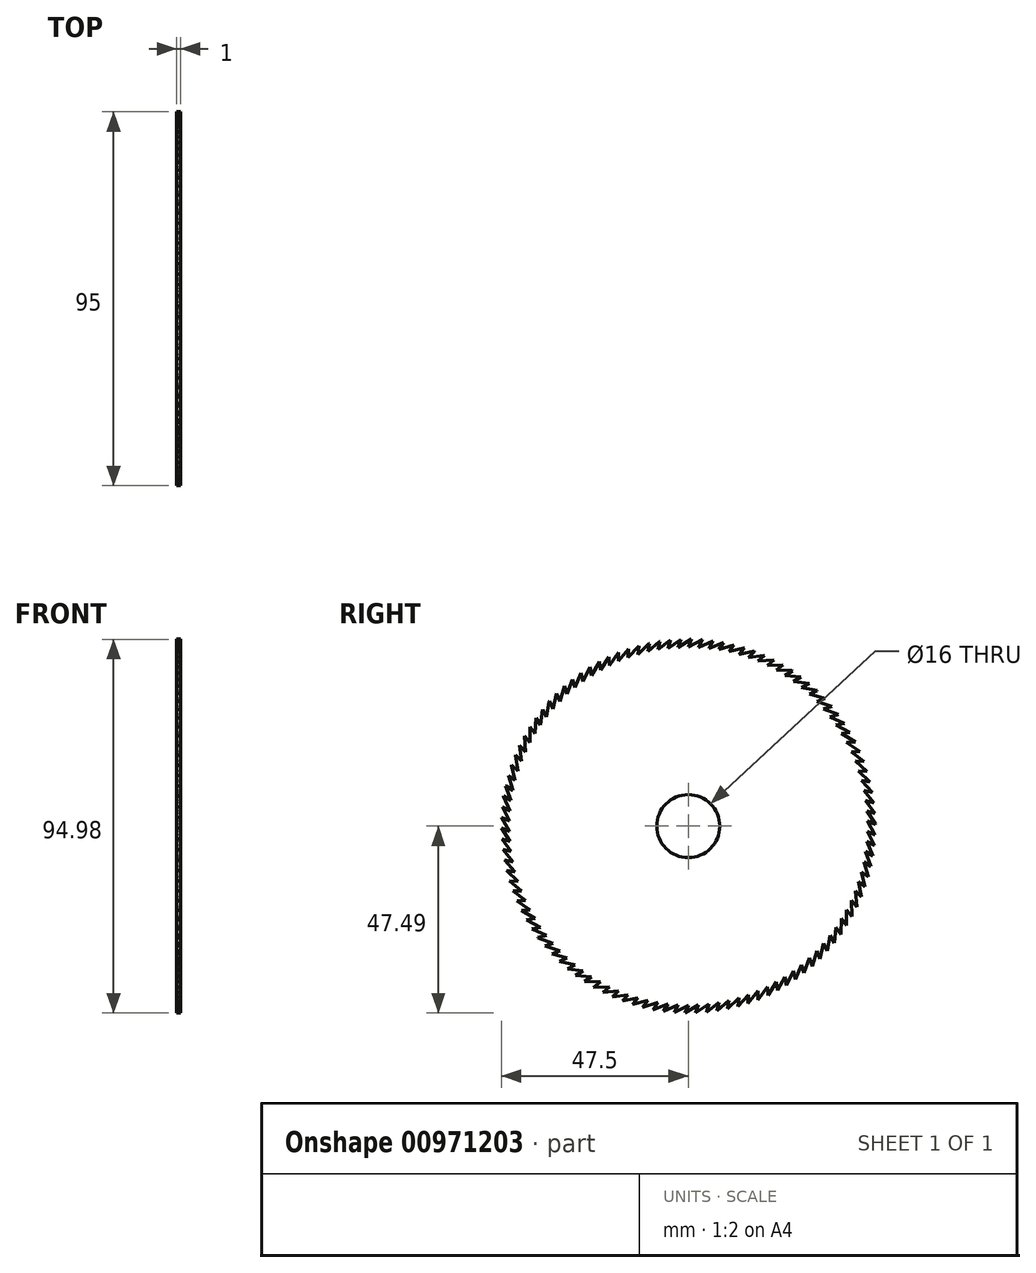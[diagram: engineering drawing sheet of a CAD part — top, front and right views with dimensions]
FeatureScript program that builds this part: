
annotation { "Feature Type Name" : "Feature", "Feature Type Description" : "" }
export const myFeature = defineFeature(function(context is Context, id is Id, definition is map)
    precondition{}
    {
        {
            var Q0;
            Q0=qCreatedBy(makeId("Right.planeOp"),FACE);
            var sketch = newSketch(context, id + "F0", { "sketchPlane" : qUnion([Q0])});
            skCircle(sketch, "E0", {"center": v(0, 0) * mm, "radius": 47.5 * mm});
            skCircle(sketch, "E1", {"center": v(0, 0) * mm, "radius": 8 * mm});
            skCircle(sketch, "E2", {"center": v(0, 0) * mm, "radius": 45.5 * mm, "construction": true});
            skLineSegment(sketch, "E3", {"start": v(0, 45.5) * mm, "end": v(0.86, 47.5) * mm});
            skLineSegment(sketch, "E4", {"start": v(0, 45.5) * mm, "end": v(3.56, 47.37) * mm});
            skArc(sketch, "E5", {"start": v(3.56, 47.37) * mm, "mid": v(2.21, 47.46) * mm, "end": v(0.86, 47.5) * mm});
            skLineSegment(sketch, "E6.1.0", {"start": v(-2.6, 45.43) * mm, "end": v(-1.85, 47.46) * mm});
            skArc(sketch, "E6.1.1", {"start": v(0.85, 47.5) * mm, "mid": v(-0.5, 47.51) * mm, "end": v(-1.85, 47.46) * mm});
            skLineSegment(sketch, "E6.1.2", {"start": v(-2.6, 45.43) * mm, "end": v(0.85, 47.5) * mm});
            skLineSegment(sketch, "E6.2.0", {"start": v(-5.19, 45.2) * mm, "end": v(-4.56, 47.28) * mm});
            skArc(sketch, "E6.2.1", {"start": v(-1.86, 47.46) * mm, "mid": v(-3.21, 47.4) * mm, "end": v(-4.56, 47.28) * mm});
            skLineSegment(sketch, "E6.2.2", {"start": v(-5.19, 45.2) * mm, "end": v(-1.86, 47.46) * mm});
            skLineSegment(sketch, "E6.3.0", {"start": v(-7.76, 44.83) * mm, "end": v(-7.25, 46.94) * mm});
            skArc(sketch, "E6.3.1", {"start": v(-4.57, 47.28) * mm, "mid": v(-5.91, 47.14) * mm, "end": v(-7.25, 46.94) * mm});
            skLineSegment(sketch, "E6.3.2", {"start": v(-7.76, 44.83) * mm, "end": v(-4.57, 47.28) * mm});
            skLineSegment(sketch, "E6.4.0", {"start": v(-10.3, 44.32) * mm, "end": v(-9.92, 46.45) * mm});
            skArc(sketch, "E6.4.1", {"start": v(-7.26, 46.94) * mm, "mid": v(-8.6, 46.73) * mm, "end": v(-9.92, 46.45) * mm});
            skLineSegment(sketch, "E6.4.2", {"start": v(-10.3, 44.32) * mm, "end": v(-7.26, 46.94) * mm});
            skLineSegment(sketch, "E6.5.0", {"start": v(-12.82, 43.66) * mm, "end": v(-12.55, 45.81) * mm});
            skArc(sketch, "E6.5.1", {"start": v(-9.93, 46.45) * mm, "mid": v(-11.25, 46.16) * mm, "end": v(-12.55, 45.81) * mm});
            skLineSegment(sketch, "E6.5.2", {"start": v(-12.82, 43.66) * mm, "end": v(-9.93, 46.45) * mm});
            skLineSegment(sketch, "E6.6.0", {"start": v(-15.3, 42.85) * mm, "end": v(-15.15, 45.02) * mm});
            skArc(sketch, "E6.6.1", {"start": v(-12.57, 45.8) * mm, "mid": v(-13.87, 45.45) * mm, "end": v(-15.15, 45.02) * mm});
            skLineSegment(sketch, "E6.6.2", {"start": v(-15.3, 42.85) * mm, "end": v(-12.57, 45.8) * mm});
            skLineSegment(sketch, "E6.7.0", {"start": v(-17.71, 41.91) * mm, "end": v(-17.7, 44.08) * mm});
            skArc(sketch, "E6.7.1", {"start": v(-15.16, 45.02) * mm, "mid": v(-16.44, 44.58) * mm, "end": v(-17.7, 44.08) * mm});
            skLineSegment(sketch, "E6.7.2", {"start": v(-17.71, 41.91) * mm, "end": v(-15.16, 45.02) * mm});
            skLineSegment(sketch, "E6.8.0", {"start": v(-20.08, 40.83) * mm, "end": v(-20.18, 43) * mm});
            skArc(sketch, "E6.8.1", {"start": v(-17.7, 44.08) * mm, "mid": v(-18.96, 43.57) * mm, "end": v(-20.18, 43) * mm});
            skLineSegment(sketch, "E6.8.2", {"start": v(-20.08, 40.83) * mm, "end": v(-17.7, 44.08) * mm});
            skLineSegment(sketch, "E6.9.0", {"start": v(-22.37, 39.62) * mm, "end": v(-22.6, 41.78) * mm});
            skArc(sketch, "E6.9.1", {"start": v(-20.2, 43) * mm, "mid": v(-21.41, 42.42) * mm, "end": v(-22.6, 41.78) * mm});
            skLineSegment(sketch, "E6.9.2", {"start": v(-22.37, 39.62) * mm, "end": v(-20.2, 43) * mm});
            skLineSegment(sketch, "E6.10.0", {"start": v(-24.6, 38.28) * mm, "end": v(-24.95, 40.42) * mm});
            skArc(sketch, "E6.10.1", {"start": v(-22.61, 41.77) * mm, "mid": v(-23.8, 41.12) * mm, "end": v(-24.95, 40.42) * mm});
            skLineSegment(sketch, "E6.10.2", {"start": v(-24.6, 38.28) * mm, "end": v(-22.61, 41.77) * mm});
            skLineSegment(sketch, "E6.11.0", {"start": v(-26.74, 36.81) * mm, "end": v(-27.22, 38.93) * mm});
            skArc(sketch, "E6.11.1", {"start": v(-24.96, 40.41) * mm, "mid": v(-26.1, 39.7) * mm, "end": v(-27.22, 38.93) * mm});
            skLineSegment(sketch, "E6.11.2", {"start": v(-26.74, 36.81) * mm, "end": v(-24.96, 40.41) * mm});
            skLineSegment(sketch, "E6.12.0", {"start": v(-28.8, 35.22) * mm, "end": v(-29.4, 37.31) * mm});
            skArc(sketch, "E6.12.1", {"start": v(-27.23, 38.92) * mm, "mid": v(-28.33, 38.14) * mm, "end": v(-29.4, 37.31) * mm});
            skLineSegment(sketch, "E6.12.2", {"start": v(-28.8, 35.22) * mm, "end": v(-27.23, 38.92) * mm});
            skLineSegment(sketch, "E6.13.0", {"start": v(-30.77, 33.52) * mm, "end": v(-31.48, 35.57) * mm});
            skArc(sketch, "E6.13.1", {"start": v(-29.4, 37.3) * mm, "mid": v(-30.46, 36.46) * mm, "end": v(-31.48, 35.57) * mm});
            skLineSegment(sketch, "E6.13.2", {"start": v(-30.77, 33.52) * mm, "end": v(-29.4, 37.3) * mm});
            skLineSegment(sketch, "E6.14.0", {"start": v(-32.63, 31.71) * mm, "end": v(-33.46, 33.72) * mm});
            skArc(sketch, "E6.14.1", {"start": v(-31.49, 35.56) * mm, "mid": v(-32.5, 34.66) * mm, "end": v(-33.46, 33.72) * mm});
            skLineSegment(sketch, "E6.14.2", {"start": v(-32.63, 31.71) * mm, "end": v(-31.49, 35.56) * mm});
            skLineSegment(sketch, "E6.15.0", {"start": v(-34.39, 29.8) * mm, "end": v(-35.33, 31.75) * mm});
            skArc(sketch, "E6.15.1", {"start": v(-33.47, 33.7) * mm, "mid": v(-34.42, 32.75) * mm, "end": v(-35.33, 31.75) * mm});
            skLineSegment(sketch, "E6.15.2", {"start": v(-34.39, 29.8) * mm, "end": v(-33.47, 33.7) * mm});
            skLineSegment(sketch, "E6.16.0", {"start": v(-36.03, 27.78) * mm, "end": v(-37.08, 29.69) * mm});
            skArc(sketch, "E6.16.1", {"start": v(-35.34, 31.74) * mm, "mid": v(-36.23, 30.73) * mm, "end": v(-37.08, 29.69) * mm});
            skLineSegment(sketch, "E6.16.2", {"start": v(-36.03, 27.78) * mm, "end": v(-35.34, 31.74) * mm});
            skLineSegment(sketch, "E6.17.0", {"start": v(-37.56, 25.68) * mm, "end": v(-38.72, 27.52) * mm});
            skArc(sketch, "E6.17.1", {"start": v(-37.1, 29.67) * mm, "mid": v(-37.93, 28.62) * mm, "end": v(-38.72, 27.52) * mm});
            skLineSegment(sketch, "E6.17.2", {"start": v(-37.56, 25.68) * mm, "end": v(-37.1, 29.67) * mm});
            skLineSegment(sketch, "E6.18.0", {"start": v(-38.96, 23.5) * mm, "end": v(-40.22, 25.26) * mm});
            skArc(sketch, "E6.18.1", {"start": v(-38.72, 27.5) * mm, "mid": v(-39.5, 26.4) * mm, "end": v(-40.22, 25.26) * mm});
            skLineSegment(sketch, "E6.18.2", {"start": v(-38.96, 23.5) * mm, "end": v(-38.72, 27.5) * mm});
            skLineSegment(sketch, "E6.19.0", {"start": v(-40.24, 21.23) * mm, "end": v(-41.6, 22.93) * mm});
            skArc(sketch, "E6.19.1", {"start": v(-40.23, 25.25) * mm, "mid": v(-40.94, 24.1) * mm, "end": v(-41.6, 22.93) * mm});
            skLineSegment(sketch, "E6.19.2", {"start": v(-40.24, 21.23) * mm, "end": v(-40.23, 25.25) * mm});
            skLineSegment(sketch, "E6.20.0", {"start": v(-41.39, 18.9) * mm, "end": v(-42.84, 20.51) * mm});
            skArc(sketch, "E6.20.1", {"start": v(-41.6, 22.91) * mm, "mid": v(-42.25, 21.73) * mm, "end": v(-42.84, 20.51) * mm});
            skLineSegment(sketch, "E6.20.2", {"start": v(-41.39, 18.9) * mm, "end": v(-41.6, 22.91) * mm});
            skLineSegment(sketch, "E6.21.0", {"start": v(-42.4, 16.5) * mm, "end": v(-43.94, 18.04) * mm});
            skArc(sketch, "E6.21.1", {"start": v(-42.85, 20.5) * mm, "mid": v(-43.43, 19.28) * mm, "end": v(-43.94, 18.04) * mm});
            skLineSegment(sketch, "E6.21.2", {"start": v(-42.4, 16.5) * mm, "end": v(-42.85, 20.5) * mm});
            skLineSegment(sketch, "E6.22.0", {"start": v(-43.27, 14.06) * mm, "end": v(-44.9, 15.5) * mm});
            skArc(sketch, "E6.22.1", {"start": v(-43.95, 18.02) * mm, "mid": v(-44.45, 16.77) * mm, "end": v(-44.9, 15.5) * mm});
            skLineSegment(sketch, "E6.22.2", {"start": v(-43.27, 14.06) * mm, "end": v(-43.95, 18.02) * mm});
            skLineSegment(sketch, "E6.23.0", {"start": v(-44, 11.57) * mm, "end": v(-45.71, 12.9) * mm});
            skArc(sketch, "E6.23.1", {"start": v(-44.9, 15.48) * mm, "mid": v(-45.34, 14.2) * mm, "end": v(-45.71, 12.9) * mm});
            skLineSegment(sketch, "E6.23.2", {"start": v(-44, 11.57) * mm, "end": v(-44.9, 15.48) * mm});
            skLineSegment(sketch, "E6.24.0", {"start": v(-44.6, 9.04) * mm, "end": v(-46.37, 10.28) * mm});
            skArc(sketch, "E6.24.1", {"start": v(-45.72, 12.9) * mm, "mid": v(-46.08, 11.6) * mm, "end": v(-46.37, 10.28) * mm});
            skLineSegment(sketch, "E6.24.2", {"start": v(-44.6, 9.04) * mm, "end": v(-45.72, 12.9) * mm});
            skLineSegment(sketch, "E6.25.0", {"start": v(-45.04, 6.48) * mm, "end": v(-46.89, 7.61) * mm});
            skArc(sketch, "E6.25.1", {"start": v(-46.38, 10.26) * mm, "mid": v(-46.66, 8.95) * mm, "end": v(-46.89, 7.61) * mm});
            skLineSegment(sketch, "E6.25.2", {"start": v(-45.04, 6.48) * mm, "end": v(-46.38, 10.26) * mm});
            skLineSegment(sketch, "E6.26.0", {"start": v(-45.33, 3.9) * mm, "end": v(-47.24, 4.92) * mm});
            skArc(sketch, "E6.26.1", {"start": v(-46.89, 7.6) * mm, "mid": v(-47.1, 6.27) * mm, "end": v(-47.24, 4.92) * mm});
            skLineSegment(sketch, "E6.26.2", {"start": v(-45.33, 3.9) * mm, "end": v(-46.89, 7.6) * mm});
            skLineSegment(sketch, "E6.27.0", {"start": v(-45.48, 1.3) * mm, "end": v(-47.45, 2.22) * mm});
            skArc(sketch, "E6.27.1", {"start": v(-47.25, 4.91) * mm, "mid": v(-47.38, 3.57) * mm, "end": v(-47.45, 2.22) * mm});
            skLineSegment(sketch, "E6.27.2", {"start": v(-45.48, 1.3) * mm, "end": v(-47.25, 4.91) * mm});
            skLineSegment(sketch, "E6.28.0", {"start": v(-45.48, -1.3) * mm, "end": v(-47.5, -0.5) * mm});
            skArc(sketch, "E6.28.1", {"start": v(-47.45, 2.2) * mm, "mid": v(-47.5, 0.86) * mm, "end": v(-47.5, -0.5) * mm});
            skLineSegment(sketch, "E6.28.2", {"start": v(-45.48, -1.3) * mm, "end": v(-47.45, 2.2) * mm});
            skLineSegment(sketch, "E6.29.0", {"start": v(-45.33, -3.9) * mm, "end": v(-47.4, -3.2) * mm});
            skArc(sketch, "E6.29.1", {"start": v(-47.5, -0.5) * mm, "mid": v(-47.48, -1.86) * mm, "end": v(-47.4, -3.2) * mm});
            skLineSegment(sketch, "E6.29.2", {"start": v(-45.33, -3.9) * mm, "end": v(-47.5, -0.5) * mm});
            skLineSegment(sketch, "E6.30.0", {"start": v(-45.04, -6.48) * mm, "end": v(-47.13, -5.9) * mm});
            skArc(sketch, "E6.30.1", {"start": v(-47.4, -3.22) * mm, "mid": v(-47.3, -4.56) * mm, "end": v(-47.13, -5.9) * mm});
            skLineSegment(sketch, "E6.30.2", {"start": v(-45.04, -6.48) * mm, "end": v(-47.4, -3.22) * mm});
            skLineSegment(sketch, "E6.31.0", {"start": v(-44.6, -9.04) * mm, "end": v(-46.72, -8.58) * mm});
            skArc(sketch, "E6.31.1", {"start": v(-47.13, -5.92) * mm, "mid": v(-46.96, -7.26) * mm, "end": v(-46.72, -8.58) * mm});
            skLineSegment(sketch, "E6.31.2", {"start": v(-44.6, -9.04) * mm, "end": v(-47.13, -5.92) * mm});
            skLineSegment(sketch, "E6.32.0", {"start": v(-44, -11.57) * mm, "end": v(-46.15, -11.24) * mm});
            skArc(sketch, "E6.32.1", {"start": v(-46.72, -8.6) * mm, "mid": v(-46.47, -9.93) * mm, "end": v(-46.15, -11.24) * mm});
            skLineSegment(sketch, "E6.32.2", {"start": v(-44, -11.57) * mm, "end": v(-46.72, -8.6) * mm});
            skLineSegment(sketch, "E6.33.0", {"start": v(-43.27, -14.06) * mm, "end": v(-45.43, -13.85) * mm});
            skArc(sketch, "E6.33.1", {"start": v(-46.15, -11.25) * mm, "mid": v(-45.82, -12.56) * mm, "end": v(-45.43, -13.85) * mm});
            skLineSegment(sketch, "E6.33.2", {"start": v(-43.27, -14.06) * mm, "end": v(-46.15, -11.25) * mm});
            skLineSegment(sketch, "E6.34.0", {"start": v(-42.4, -16.5) * mm, "end": v(-44.57, -16.43) * mm});
            skArc(sketch, "E6.34.1", {"start": v(-45.43, -13.87) * mm, "mid": v(-45.03, -15.16) * mm, "end": v(-44.57, -16.43) * mm});
            skLineSegment(sketch, "E6.34.2", {"start": v(-42.4, -16.5) * mm, "end": v(-45.43, -13.87) * mm});
            skLineSegment(sketch, "E6.35.0", {"start": v(-41.39, -18.9) * mm, "end": v(-43.56, -18.94) * mm});
            skArc(sketch, "E6.35.1", {"start": v(-44.56, -16.44) * mm, "mid": v(-44.1, -17.7) * mm, "end": v(-43.56, -18.94) * mm});
            skLineSegment(sketch, "E6.35.2", {"start": v(-41.39, -18.9) * mm, "end": v(-44.56, -16.44) * mm});
            skLineSegment(sketch, "E6.36.0", {"start": v(-40.24, -21.23) * mm, "end": v(-42.4, -21.4) * mm});
            skArc(sketch, "E6.36.1", {"start": v(-43.55, -18.96) * mm, "mid": v(-43, -20.2) * mm, "end": v(-42.4, -21.4) * mm});
            skLineSegment(sketch, "E6.36.2", {"start": v(-40.24, -21.23) * mm, "end": v(-43.55, -18.96) * mm});
            skLineSegment(sketch, "E6.37.0", {"start": v(-38.96, -23.5) * mm, "end": v(-41.12, -23.78) * mm});
            skArc(sketch, "E6.37.1", {"start": v(-42.4, -21.41) * mm, "mid": v(-41.79, -22.61) * mm, "end": v(-41.12, -23.78) * mm});
            skLineSegment(sketch, "E6.37.2", {"start": v(-38.96, -23.5) * mm, "end": v(-42.4, -21.41) * mm});
            skLineSegment(sketch, "E6.38.0", {"start": v(-37.56, -25.68) * mm, "end": v(-39.7, -26.1) * mm});
            skArc(sketch, "E6.38.1", {"start": v(-41.1, -23.8) * mm, "mid": v(-40.43, -24.96) * mm, "end": v(-39.7, -26.1) * mm});
            skLineSegment(sketch, "E6.38.2", {"start": v(-37.56, -25.68) * mm, "end": v(-41.1, -23.8) * mm});
            skLineSegment(sketch, "E6.39.0", {"start": v(-36.03, -27.78) * mm, "end": v(-38.14, -28.32) * mm});
            skArc(sketch, "E6.39.1", {"start": v(-39.68, -26.1) * mm, "mid": v(-38.94, -27.23) * mm, "end": v(-38.14, -28.32) * mm});
            skLineSegment(sketch, "E6.39.2", {"start": v(-36.03, -27.78) * mm, "end": v(-39.68, -26.1) * mm});
            skLineSegment(sketch, "E6.40.0", {"start": v(-34.39, -29.8) * mm, "end": v(-36.46, -30.45) * mm});
            skArc(sketch, "E6.40.1", {"start": v(-38.13, -28.33) * mm, "mid": v(-37.32, -29.4) * mm, "end": v(-36.46, -30.45) * mm});
            skLineSegment(sketch, "E6.40.2", {"start": v(-34.39, -29.8) * mm, "end": v(-38.13, -28.33) * mm});
            skLineSegment(sketch, "E6.41.0", {"start": v(-32.63, -31.71) * mm, "end": v(-34.66, -32.48) * mm});
            skArc(sketch, "E6.41.1", {"start": v(-36.45, -30.46) * mm, "mid": v(-35.58, -31.5) * mm, "end": v(-34.66, -32.48) * mm});
            skLineSegment(sketch, "E6.41.2", {"start": v(-32.63, -31.71) * mm, "end": v(-36.45, -30.46) * mm});
            skLineSegment(sketch, "E6.42.0", {"start": v(-30.77, -33.52) * mm, "end": v(-32.75, -34.4) * mm});
            skArc(sketch, "E6.42.1", {"start": v(-34.65, -32.5) * mm, "mid": v(-33.72, -33.47) * mm, "end": v(-32.75, -34.4) * mm});
            skLineSegment(sketch, "E6.42.2", {"start": v(-30.77, -33.52) * mm, "end": v(-34.65, -32.5) * mm});
            skLineSegment(sketch, "E6.43.0", {"start": v(-28.8, -35.22) * mm, "end": v(-30.73, -36.22) * mm});
            skArc(sketch, "E6.43.1", {"start": v(-32.74, -34.42) * mm, "mid": v(-31.76, -35.34) * mm, "end": v(-30.73, -36.22) * mm});
            skLineSegment(sketch, "E6.43.2", {"start": v(-28.8, -35.22) * mm, "end": v(-32.74, -34.42) * mm});
            skLineSegment(sketch, "E6.44.0", {"start": v(-26.74, -36.81) * mm, "end": v(-28.61, -37.91) * mm});
            skArc(sketch, "E6.44.1", {"start": v(-30.72, -36.23) * mm, "mid": v(-29.69, -37.1) * mm, "end": v(-28.61, -37.91) * mm});
            skLineSegment(sketch, "E6.44.2", {"start": v(-26.74, -36.81) * mm, "end": v(-30.72, -36.23) * mm});
            skLineSegment(sketch, "E6.45.0", {"start": v(-24.6, -38.28) * mm, "end": v(-26.4, -39.49) * mm});
            skArc(sketch, "E6.45.1", {"start": v(-28.6, -37.92) * mm, "mid": v(-27.52, -38.73) * mm, "end": v(-26.4, -39.49) * mm});
            skLineSegment(sketch, "E6.45.2", {"start": v(-24.6, -38.28) * mm, "end": v(-28.6, -37.92) * mm});
            skLineSegment(sketch, "E6.46.0", {"start": v(-22.37, -39.62) * mm, "end": v(-24.1, -40.93) * mm});
            skArc(sketch, "E6.46.1", {"start": v(-26.4, -39.5) * mm, "mid": v(-25.27, -40.24) * mm, "end": v(-24.1, -40.93) * mm});
            skLineSegment(sketch, "E6.46.2", {"start": v(-22.37, -39.62) * mm, "end": v(-26.4, -39.5) * mm});
            skLineSegment(sketch, "E6.47.0", {"start": v(-20.08, -40.83) * mm, "end": v(-21.73, -42.24) * mm});
            skArc(sketch, "E6.47.1", {"start": v(-24.1, -40.94) * mm, "mid": v(-22.93, -41.62) * mm, "end": v(-21.73, -42.24) * mm});
            skLineSegment(sketch, "E6.47.2", {"start": v(-20.08, -40.83) * mm, "end": v(-24.1, -40.94) * mm});
            skLineSegment(sketch, "E6.48.0", {"start": v(-17.71, -41.91) * mm, "end": v(-19.28, -43.4) * mm});
            skArc(sketch, "E6.48.1", {"start": v(-21.72, -42.24) * mm, "mid": v(-20.51, -42.86) * mm, "end": v(-19.28, -43.4) * mm});
            skLineSegment(sketch, "E6.48.2", {"start": v(-17.71, -41.91) * mm, "end": v(-21.72, -42.24) * mm});
            skLineSegment(sketch, "E6.49.0", {"start": v(-15.3, -42.85) * mm, "end": v(-16.77, -44.44) * mm});
            skArc(sketch, "E6.49.1", {"start": v(-19.27, -43.42) * mm, "mid": v(-18.03, -43.96) * mm, "end": v(-16.77, -44.44) * mm});
            skLineSegment(sketch, "E6.49.2", {"start": v(-15.3, -42.85) * mm, "end": v(-19.27, -43.42) * mm});
            skLineSegment(sketch, "E6.50.0", {"start": v(-12.82, -43.66) * mm, "end": v(-14.2, -45.32) * mm});
            skArc(sketch, "E6.50.1", {"start": v(-16.76, -44.45) * mm, "mid": v(-15.5, -44.92) * mm, "end": v(-14.2, -45.32) * mm});
            skLineSegment(sketch, "E6.50.2", {"start": v(-12.82, -43.66) * mm, "end": v(-16.76, -44.45) * mm});
            skLineSegment(sketch, "E6.51.0", {"start": v(-10.3, -44.32) * mm, "end": v(-11.6, -46.06) * mm});
            skArc(sketch, "E6.51.1", {"start": v(-14.2, -45.33) * mm, "mid": v(-12.9, -45.73) * mm, "end": v(-11.6, -46.06) * mm});
            skLineSegment(sketch, "E6.51.2", {"start": v(-10.3, -44.32) * mm, "end": v(-14.2, -45.33) * mm});
            skLineSegment(sketch, "E6.52.0", {"start": v(-7.76, -44.83) * mm, "end": v(-8.95, -46.65) * mm});
            skArc(sketch, "E6.52.1", {"start": v(-11.58, -46.07) * mm, "mid": v(-10.27, -46.39) * mm, "end": v(-8.95, -46.65) * mm});
            skLineSegment(sketch, "E6.52.2", {"start": v(-7.76, -44.83) * mm, "end": v(-11.58, -46.07) * mm});
            skLineSegment(sketch, "E6.53.0", {"start": v(-5.19, -45.2) * mm, "end": v(-6.27, -47.08) * mm});
            skArc(sketch, "E6.53.1", {"start": v(-8.94, -46.65) * mm, "mid": v(-7.6, -46.9) * mm, "end": v(-6.27, -47.08) * mm});
            skLineSegment(sketch, "E6.53.2", {"start": v(-5.19, -45.2) * mm, "end": v(-8.94, -46.65) * mm});
            skLineSegment(sketch, "E6.54.0", {"start": v(-2.6, -45.43) * mm, "end": v(-3.57, -47.37) * mm});
            skArc(sketch, "E6.54.1", {"start": v(-6.26, -47.09) * mm, "mid": v(-4.92, -47.26) * mm, "end": v(-3.57, -47.37) * mm});
            skLineSegment(sketch, "E6.54.2", {"start": v(-2.6, -45.43) * mm, "end": v(-6.26, -47.09) * mm});
            skLineSegment(sketch, "E6.55.0", {"start": v(0, -45.5) * mm, "end": v(-0.86, -47.5) * mm});
            skArc(sketch, "E6.55.1", {"start": v(-3.56, -47.37) * mm, "mid": v(-2.21, -47.46) * mm, "end": v(-0.86, -47.5) * mm});
            skLineSegment(sketch, "E6.55.2", {"start": v(0, -45.5) * mm, "end": v(-3.56, -47.37) * mm});
            skLineSegment(sketch, "E6.56.0", {"start": v(2.6, -45.43) * mm, "end": v(1.85, -47.46) * mm});
            skArc(sketch, "E6.56.1", {"start": v(-0.85, -47.5) * mm, "mid": v(0.5, -47.51) * mm, "end": v(1.85, -47.46) * mm});
            skLineSegment(sketch, "E6.56.2", {"start": v(2.6, -45.43) * mm, "end": v(-0.85, -47.5) * mm});
            skLineSegment(sketch, "E6.57.0", {"start": v(5.19, -45.2) * mm, "end": v(4.56, -47.28) * mm});
            skArc(sketch, "E6.57.1", {"start": v(1.86, -47.46) * mm, "mid": v(3.21, -47.4) * mm, "end": v(4.56, -47.28) * mm});
            skLineSegment(sketch, "E6.57.2", {"start": v(5.19, -45.2) * mm, "end": v(1.86, -47.46) * mm});
            skLineSegment(sketch, "E6.58.0", {"start": v(7.76, -44.83) * mm, "end": v(7.25, -46.94) * mm});
            skArc(sketch, "E6.58.1", {"start": v(4.57, -47.28) * mm, "mid": v(5.91, -47.14) * mm, "end": v(7.25, -46.94) * mm});
            skLineSegment(sketch, "E6.58.2", {"start": v(7.76, -44.83) * mm, "end": v(4.57, -47.28) * mm});
            skLineSegment(sketch, "E6.59.0", {"start": v(10.3, -44.32) * mm, "end": v(9.92, -46.45) * mm});
            skArc(sketch, "E6.59.1", {"start": v(7.26, -46.94) * mm, "mid": v(8.6, -46.73) * mm, "end": v(9.92, -46.45) * mm});
            skLineSegment(sketch, "E6.59.2", {"start": v(10.3, -44.32) * mm, "end": v(7.26, -46.94) * mm});
            skLineSegment(sketch, "E6.60.0", {"start": v(12.82, -43.66) * mm, "end": v(12.55, -45.81) * mm});
            skArc(sketch, "E6.60.1", {"start": v(9.93, -46.45) * mm, "mid": v(11.25, -46.16) * mm, "end": v(12.55, -45.81) * mm});
            skLineSegment(sketch, "E6.60.2", {"start": v(12.82, -43.66) * mm, "end": v(9.93, -46.45) * mm});
            skLineSegment(sketch, "E6.61.0", {"start": v(15.3, -42.85) * mm, "end": v(15.15, -45.02) * mm});
            skArc(sketch, "E6.61.1", {"start": v(12.57, -45.8) * mm, "mid": v(13.87, -45.45) * mm, "end": v(15.15, -45.02) * mm});
            skLineSegment(sketch, "E6.61.2", {"start": v(15.3, -42.85) * mm, "end": v(12.57, -45.8) * mm});
            skLineSegment(sketch, "E6.62.0", {"start": v(17.71, -41.91) * mm, "end": v(17.7, -44.08) * mm});
            skArc(sketch, "E6.62.1", {"start": v(15.16, -45.02) * mm, "mid": v(16.44, -44.58) * mm, "end": v(17.7, -44.08) * mm});
            skLineSegment(sketch, "E6.62.2", {"start": v(17.71, -41.91) * mm, "end": v(15.16, -45.02) * mm});
            skLineSegment(sketch, "E6.63.0", {"start": v(20.08, -40.83) * mm, "end": v(20.18, -43) * mm});
            skArc(sketch, "E6.63.1", {"start": v(17.7, -44.08) * mm, "mid": v(18.96, -43.57) * mm, "end": v(20.18, -43) * mm});
            skLineSegment(sketch, "E6.63.2", {"start": v(20.08, -40.83) * mm, "end": v(17.7, -44.08) * mm});
            skLineSegment(sketch, "E6.64.0", {"start": v(22.37, -39.62) * mm, "end": v(22.6, -41.78) * mm});
            skArc(sketch, "E6.64.1", {"start": v(20.2, -43) * mm, "mid": v(21.41, -42.42) * mm, "end": v(22.6, -41.78) * mm});
            skLineSegment(sketch, "E6.64.2", {"start": v(22.37, -39.62) * mm, "end": v(20.2, -43) * mm});
            skLineSegment(sketch, "E6.65.0", {"start": v(24.6, -38.28) * mm, "end": v(24.95, -40.42) * mm});
            skArc(sketch, "E6.65.1", {"start": v(22.61, -41.77) * mm, "mid": v(23.8, -41.12) * mm, "end": v(24.95, -40.42) * mm});
            skLineSegment(sketch, "E6.65.2", {"start": v(24.6, -38.28) * mm, "end": v(22.61, -41.77) * mm});
            skLineSegment(sketch, "E6.66.0", {"start": v(26.74, -36.81) * mm, "end": v(27.22, -38.93) * mm});
            skArc(sketch, "E6.66.1", {"start": v(24.96, -40.41) * mm, "mid": v(26.1, -39.7) * mm, "end": v(27.22, -38.93) * mm});
            skLineSegment(sketch, "E6.66.2", {"start": v(26.74, -36.81) * mm, "end": v(24.96, -40.41) * mm});
            skLineSegment(sketch, "E6.67.0", {"start": v(28.8, -35.22) * mm, "end": v(29.4, -37.31) * mm});
            skArc(sketch, "E6.67.1", {"start": v(27.23, -38.92) * mm, "mid": v(28.33, -38.14) * mm, "end": v(29.4, -37.31) * mm});
            skLineSegment(sketch, "E6.67.2", {"start": v(28.8, -35.22) * mm, "end": v(27.23, -38.92) * mm});
            skLineSegment(sketch, "E6.68.0", {"start": v(30.77, -33.52) * mm, "end": v(31.48, -35.57) * mm});
            skArc(sketch, "E6.68.1", {"start": v(29.4, -37.3) * mm, "mid": v(30.46, -36.46) * mm, "end": v(31.48, -35.57) * mm});
            skLineSegment(sketch, "E6.68.2", {"start": v(30.77, -33.52) * mm, "end": v(29.4, -37.3) * mm});
            skLineSegment(sketch, "E6.69.0", {"start": v(32.63, -31.71) * mm, "end": v(33.46, -33.72) * mm});
            skArc(sketch, "E6.69.1", {"start": v(31.49, -35.56) * mm, "mid": v(32.5, -34.66) * mm, "end": v(33.46, -33.72) * mm});
            skLineSegment(sketch, "E6.69.2", {"start": v(32.63, -31.71) * mm, "end": v(31.49, -35.56) * mm});
            skLineSegment(sketch, "E6.70.0", {"start": v(34.39, -29.8) * mm, "end": v(35.33, -31.75) * mm});
            skArc(sketch, "E6.70.1", {"start": v(33.47, -33.7) * mm, "mid": v(34.42, -32.75) * mm, "end": v(35.33, -31.75) * mm});
            skLineSegment(sketch, "E6.70.2", {"start": v(34.39, -29.8) * mm, "end": v(33.47, -33.7) * mm});
            skLineSegment(sketch, "E6.71.0", {"start": v(36.03, -27.78) * mm, "end": v(37.08, -29.69) * mm});
            skArc(sketch, "E6.71.1", {"start": v(35.34, -31.74) * mm, "mid": v(36.23, -30.73) * mm, "end": v(37.08, -29.69) * mm});
            skLineSegment(sketch, "E6.71.2", {"start": v(36.03, -27.78) * mm, "end": v(35.34, -31.74) * mm});
            skLineSegment(sketch, "E6.72.0", {"start": v(37.56, -25.68) * mm, "end": v(38.72, -27.52) * mm});
            skArc(sketch, "E6.72.1", {"start": v(37.1, -29.67) * mm, "mid": v(37.93, -28.62) * mm, "end": v(38.72, -27.52) * mm});
            skLineSegment(sketch, "E6.72.2", {"start": v(37.56, -25.68) * mm, "end": v(37.1, -29.67) * mm});
            skLineSegment(sketch, "E6.73.0", {"start": v(38.96, -23.5) * mm, "end": v(40.22, -25.26) * mm});
            skArc(sketch, "E6.73.1", {"start": v(38.72, -27.5) * mm, "mid": v(39.5, -26.4) * mm, "end": v(40.22, -25.26) * mm});
            skLineSegment(sketch, "E6.73.2", {"start": v(38.96, -23.5) * mm, "end": v(38.72, -27.5) * mm});
            skLineSegment(sketch, "E6.74.0", {"start": v(40.24, -21.23) * mm, "end": v(41.6, -22.93) * mm});
            skArc(sketch, "E6.74.1", {"start": v(40.23, -25.25) * mm, "mid": v(40.94, -24.1) * mm, "end": v(41.6, -22.93) * mm});
            skLineSegment(sketch, "E6.74.2", {"start": v(40.24, -21.23) * mm, "end": v(40.23, -25.25) * mm});
            skLineSegment(sketch, "E6.75.0", {"start": v(41.39, -18.9) * mm, "end": v(42.84, -20.51) * mm});
            skArc(sketch, "E6.75.1", {"start": v(41.6, -22.91) * mm, "mid": v(42.25, -21.73) * mm, "end": v(42.84, -20.51) * mm});
            skLineSegment(sketch, "E6.75.2", {"start": v(41.39, -18.9) * mm, "end": v(41.6, -22.91) * mm});
            skLineSegment(sketch, "E6.76.0", {"start": v(42.4, -16.5) * mm, "end": v(43.94, -18.04) * mm});
            skArc(sketch, "E6.76.1", {"start": v(42.85, -20.5) * mm, "mid": v(43.43, -19.28) * mm, "end": v(43.94, -18.04) * mm});
            skLineSegment(sketch, "E6.76.2", {"start": v(42.4, -16.5) * mm, "end": v(42.85, -20.5) * mm});
            skLineSegment(sketch, "E6.77.0", {"start": v(43.27, -14.06) * mm, "end": v(44.9, -15.5) * mm});
            skArc(sketch, "E6.77.1", {"start": v(43.95, -18.02) * mm, "mid": v(44.45, -16.77) * mm, "end": v(44.9, -15.5) * mm});
            skLineSegment(sketch, "E6.77.2", {"start": v(43.27, -14.06) * mm, "end": v(43.95, -18.02) * mm});
            skLineSegment(sketch, "E6.78.0", {"start": v(44, -11.57) * mm, "end": v(45.71, -12.9) * mm});
            skArc(sketch, "E6.78.1", {"start": v(44.9, -15.48) * mm, "mid": v(45.34, -14.2) * mm, "end": v(45.71, -12.9) * mm});
            skLineSegment(sketch, "E6.78.2", {"start": v(44, -11.57) * mm, "end": v(44.9, -15.48) * mm});
            skLineSegment(sketch, "E6.79.0", {"start": v(44.6, -9.04) * mm, "end": v(46.37, -10.28) * mm});
            skArc(sketch, "E6.79.1", {"start": v(45.72, -12.9) * mm, "mid": v(46.08, -11.6) * mm, "end": v(46.37, -10.28) * mm});
            skLineSegment(sketch, "E6.79.2", {"start": v(44.6, -9.04) * mm, "end": v(45.72, -12.9) * mm});
            skLineSegment(sketch, "E6.80.0", {"start": v(45.04, -6.48) * mm, "end": v(46.89, -7.61) * mm});
            skArc(sketch, "E6.80.1", {"start": v(46.38, -10.26) * mm, "mid": v(46.66, -8.95) * mm, "end": v(46.89, -7.61) * mm});
            skLineSegment(sketch, "E6.80.2", {"start": v(45.04, -6.48) * mm, "end": v(46.38, -10.26) * mm});
            skLineSegment(sketch, "E6.81.0", {"start": v(45.33, -3.9) * mm, "end": v(47.24, -4.92) * mm});
            skArc(sketch, "E6.81.1", {"start": v(46.89, -7.6) * mm, "mid": v(47.1, -6.27) * mm, "end": v(47.24, -4.92) * mm});
            skLineSegment(sketch, "E6.81.2", {"start": v(45.33, -3.9) * mm, "end": v(46.89, -7.6) * mm});
            skLineSegment(sketch, "E6.82.0", {"start": v(45.48, -1.3) * mm, "end": v(47.45, -2.22) * mm});
            skArc(sketch, "E6.82.1", {"start": v(47.25, -4.91) * mm, "mid": v(47.38, -3.57) * mm, "end": v(47.45, -2.22) * mm});
            skLineSegment(sketch, "E6.82.2", {"start": v(45.48, -1.3) * mm, "end": v(47.25, -4.91) * mm});
            skLineSegment(sketch, "E6.83.0", {"start": v(45.48, 1.3) * mm, "end": v(47.5, 0.5) * mm});
            skArc(sketch, "E6.83.1", {"start": v(47.45, -2.2) * mm, "mid": v(47.5, -0.86) * mm, "end": v(47.5, 0.5) * mm});
            skLineSegment(sketch, "E6.83.2", {"start": v(45.48, 1.3) * mm, "end": v(47.45, -2.2) * mm});
            skLineSegment(sketch, "E6.84.0", {"start": v(45.33, 3.9) * mm, "end": v(47.4, 3.2) * mm});
            skArc(sketch, "E6.84.1", {"start": v(47.5, 0.5) * mm, "mid": v(47.48, 1.86) * mm, "end": v(47.4, 3.2) * mm});
            skLineSegment(sketch, "E6.84.2", {"start": v(45.33, 3.9) * mm, "end": v(47.5, 0.5) * mm});
            skLineSegment(sketch, "E6.85.0", {"start": v(45.04, 6.48) * mm, "end": v(47.13, 5.9) * mm});
            skArc(sketch, "E6.85.1", {"start": v(47.4, 3.22) * mm, "mid": v(47.3, 4.56) * mm, "end": v(47.13, 5.9) * mm});
            skLineSegment(sketch, "E6.85.2", {"start": v(45.04, 6.48) * mm, "end": v(47.4, 3.22) * mm});
            skLineSegment(sketch, "E6.86.0", {"start": v(44.6, 9.04) * mm, "end": v(46.72, 8.58) * mm});
            skArc(sketch, "E6.86.1", {"start": v(47.13, 5.92) * mm, "mid": v(46.96, 7.26) * mm, "end": v(46.72, 8.58) * mm});
            skLineSegment(sketch, "E6.86.2", {"start": v(44.6, 9.04) * mm, "end": v(47.13, 5.92) * mm});
            skLineSegment(sketch, "E6.87.0", {"start": v(44, 11.57) * mm, "end": v(46.15, 11.24) * mm});
            skArc(sketch, "E6.87.1", {"start": v(46.72, 8.6) * mm, "mid": v(46.47, 9.93) * mm, "end": v(46.15, 11.24) * mm});
            skLineSegment(sketch, "E6.87.2", {"start": v(44, 11.57) * mm, "end": v(46.72, 8.6) * mm});
            skLineSegment(sketch, "E6.88.0", {"start": v(43.27, 14.06) * mm, "end": v(45.43, 13.85) * mm});
            skArc(sketch, "E6.88.1", {"start": v(46.15, 11.25) * mm, "mid": v(45.82, 12.56) * mm, "end": v(45.43, 13.85) * mm});
            skLineSegment(sketch, "E6.88.2", {"start": v(43.27, 14.06) * mm, "end": v(46.15, 11.25) * mm});
            skLineSegment(sketch, "E6.89.0", {"start": v(42.4, 16.5) * mm, "end": v(44.57, 16.43) * mm});
            skArc(sketch, "E6.89.1", {"start": v(45.43, 13.87) * mm, "mid": v(45.03, 15.16) * mm, "end": v(44.57, 16.43) * mm});
            skLineSegment(sketch, "E6.89.2", {"start": v(42.4, 16.5) * mm, "end": v(45.43, 13.87) * mm});
            skLineSegment(sketch, "E6.90.0", {"start": v(41.39, 18.9) * mm, "end": v(43.56, 18.94) * mm});
            skArc(sketch, "E6.90.1", {"start": v(44.56, 16.44) * mm, "mid": v(44.1, 17.7) * mm, "end": v(43.56, 18.94) * mm});
            skLineSegment(sketch, "E6.90.2", {"start": v(41.39, 18.9) * mm, "end": v(44.56, 16.44) * mm});
            skLineSegment(sketch, "E6.91.0", {"start": v(40.24, 21.23) * mm, "end": v(42.4, 21.4) * mm});
            skArc(sketch, "E6.91.1", {"start": v(43.55, 18.96) * mm, "mid": v(43, 20.2) * mm, "end": v(42.4, 21.4) * mm});
            skLineSegment(sketch, "E6.91.2", {"start": v(40.24, 21.23) * mm, "end": v(43.55, 18.96) * mm});
            skLineSegment(sketch, "E6.92.0", {"start": v(38.96, 23.5) * mm, "end": v(41.12, 23.78) * mm});
            skArc(sketch, "E6.92.1", {"start": v(42.4, 21.41) * mm, "mid": v(41.79, 22.61) * mm, "end": v(41.12, 23.78) * mm});
            skLineSegment(sketch, "E6.92.2", {"start": v(38.96, 23.5) * mm, "end": v(42.4, 21.41) * mm});
            skLineSegment(sketch, "E6.93.0", {"start": v(37.56, 25.68) * mm, "end": v(39.7, 26.1) * mm});
            skArc(sketch, "E6.93.1", {"start": v(41.1, 23.8) * mm, "mid": v(40.43, 24.96) * mm, "end": v(39.7, 26.1) * mm});
            skLineSegment(sketch, "E6.93.2", {"start": v(37.56, 25.68) * mm, "end": v(41.1, 23.8) * mm});
            skLineSegment(sketch, "E6.94.0", {"start": v(36.03, 27.78) * mm, "end": v(38.14, 28.32) * mm});
            skArc(sketch, "E6.94.1", {"start": v(39.68, 26.1) * mm, "mid": v(38.94, 27.23) * mm, "end": v(38.14, 28.32) * mm});
            skLineSegment(sketch, "E6.94.2", {"start": v(36.03, 27.78) * mm, "end": v(39.68, 26.1) * mm});
            skLineSegment(sketch, "E6.95.0", {"start": v(34.39, 29.8) * mm, "end": v(36.46, 30.45) * mm});
            skArc(sketch, "E6.95.1", {"start": v(38.13, 28.33) * mm, "mid": v(37.32, 29.4) * mm, "end": v(36.46, 30.45) * mm});
            skLineSegment(sketch, "E6.95.2", {"start": v(34.39, 29.8) * mm, "end": v(38.13, 28.33) * mm});
            skLineSegment(sketch, "E6.96.0", {"start": v(32.63, 31.71) * mm, "end": v(34.66, 32.48) * mm});
            skArc(sketch, "E6.96.1", {"start": v(36.45, 30.46) * mm, "mid": v(35.58, 31.5) * mm, "end": v(34.66, 32.48) * mm});
            skLineSegment(sketch, "E6.96.2", {"start": v(32.63, 31.71) * mm, "end": v(36.45, 30.46) * mm});
            skLineSegment(sketch, "E6.97.0", {"start": v(30.77, 33.52) * mm, "end": v(32.75, 34.4) * mm});
            skArc(sketch, "E6.97.1", {"start": v(34.65, 32.5) * mm, "mid": v(33.72, 33.47) * mm, "end": v(32.75, 34.4) * mm});
            skLineSegment(sketch, "E6.97.2", {"start": v(30.77, 33.52) * mm, "end": v(34.65, 32.5) * mm});
            skLineSegment(sketch, "E6.98.0", {"start": v(28.8, 35.22) * mm, "end": v(30.73, 36.22) * mm});
            skArc(sketch, "E6.98.1", {"start": v(32.74, 34.42) * mm, "mid": v(31.76, 35.34) * mm, "end": v(30.73, 36.22) * mm});
            skLineSegment(sketch, "E6.98.2", {"start": v(28.8, 35.22) * mm, "end": v(32.74, 34.42) * mm});
            skLineSegment(sketch, "E6.99.0", {"start": v(26.74, 36.81) * mm, "end": v(28.61, 37.91) * mm});
            skArc(sketch, "E6.99.1", {"start": v(30.72, 36.23) * mm, "mid": v(29.69, 37.1) * mm, "end": v(28.61, 37.91) * mm});
            skLineSegment(sketch, "E6.99.2", {"start": v(26.74, 36.81) * mm, "end": v(30.72, 36.23) * mm});
            skLineSegment(sketch, "E6.100.0", {"start": v(24.6, 38.28) * mm, "end": v(26.4, 39.49) * mm});
            skArc(sketch, "E6.100.1", {"start": v(28.6, 37.92) * mm, "mid": v(27.52, 38.73) * mm, "end": v(26.4, 39.49) * mm});
            skLineSegment(sketch, "E6.100.2", {"start": v(24.6, 38.28) * mm, "end": v(28.6, 37.92) * mm});
            skLineSegment(sketch, "E6.101.0", {"start": v(22.37, 39.62) * mm, "end": v(24.1, 40.93) * mm});
            skArc(sketch, "E6.101.1", {"start": v(26.4, 39.5) * mm, "mid": v(25.27, 40.24) * mm, "end": v(24.1, 40.93) * mm});
            skLineSegment(sketch, "E6.101.2", {"start": v(22.37, 39.62) * mm, "end": v(26.4, 39.5) * mm});
            skLineSegment(sketch, "E6.102.0", {"start": v(20.08, 40.83) * mm, "end": v(21.73, 42.24) * mm});
            skArc(sketch, "E6.102.1", {"start": v(24.1, 40.94) * mm, "mid": v(22.93, 41.62) * mm, "end": v(21.73, 42.24) * mm});
            skLineSegment(sketch, "E6.102.2", {"start": v(20.08, 40.83) * mm, "end": v(24.1, 40.94) * mm});
            skLineSegment(sketch, "E6.103.0", {"start": v(17.71, 41.91) * mm, "end": v(19.28, 43.4) * mm});
            skArc(sketch, "E6.103.1", {"start": v(21.72, 42.24) * mm, "mid": v(20.51, 42.86) * mm, "end": v(19.28, 43.4) * mm});
            skLineSegment(sketch, "E6.103.2", {"start": v(17.71, 41.91) * mm, "end": v(21.72, 42.24) * mm});
            skLineSegment(sketch, "E6.104.0", {"start": v(15.3, 42.85) * mm, "end": v(16.77, 44.44) * mm});
            skArc(sketch, "E6.104.1", {"start": v(19.27, 43.42) * mm, "mid": v(18.03, 43.96) * mm, "end": v(16.77, 44.44) * mm});
            skLineSegment(sketch, "E6.104.2", {"start": v(15.3, 42.85) * mm, "end": v(19.27, 43.42) * mm});
            skLineSegment(sketch, "E6.105.0", {"start": v(12.82, 43.66) * mm, "end": v(14.2, 45.32) * mm});
            skArc(sketch, "E6.105.1", {"start": v(16.76, 44.45) * mm, "mid": v(15.5, 44.92) * mm, "end": v(14.2, 45.32) * mm});
            skLineSegment(sketch, "E6.105.2", {"start": v(12.82, 43.66) * mm, "end": v(16.76, 44.45) * mm});
            skLineSegment(sketch, "E6.106.0", {"start": v(10.3, 44.32) * mm, "end": v(11.6, 46.06) * mm});
            skArc(sketch, "E6.106.1", {"start": v(14.2, 45.33) * mm, "mid": v(12.9, 45.73) * mm, "end": v(11.6, 46.06) * mm});
            skLineSegment(sketch, "E6.106.2", {"start": v(10.3, 44.32) * mm, "end": v(14.2, 45.33) * mm});
            skLineSegment(sketch, "E6.107.0", {"start": v(7.76, 44.83) * mm, "end": v(8.95, 46.65) * mm});
            skArc(sketch, "E6.107.1", {"start": v(11.58, 46.07) * mm, "mid": v(10.27, 46.39) * mm, "end": v(8.95, 46.65) * mm});
            skLineSegment(sketch, "E6.107.2", {"start": v(7.76, 44.83) * mm, "end": v(11.58, 46.07) * mm});
            skLineSegment(sketch, "E6.108.0", {"start": v(5.19, 45.2) * mm, "end": v(6.27, 47.08) * mm});
            skArc(sketch, "E6.108.1", {"start": v(8.94, 46.65) * mm, "mid": v(7.6, 46.9) * mm, "end": v(6.27, 47.08) * mm});
            skLineSegment(sketch, "E6.108.2", {"start": v(5.19, 45.2) * mm, "end": v(8.94, 46.65) * mm});
            skLineSegment(sketch, "E6.109.0", {"start": v(2.6, 45.43) * mm, "end": v(3.57, 47.37) * mm});
            skArc(sketch, "E6.109.1", {"start": v(6.26, 47.09) * mm, "mid": v(4.92, 47.26) * mm, "end": v(3.57, 47.37) * mm});
            skLineSegment(sketch, "E6.109.2", {"start": v(2.6, 45.43) * mm, "end": v(6.26, 47.09) * mm});
            skSolve(sketch);
        }
        {
            var Q0;
            Q0=makeQuery(id+"F0.imprint","IMPRINT",FACE,{"disambiguationData":[TD([[makeQuery(id+"F0.imprint","IMPRINT",EDGE,{"derivedFrom":sQuery(id+"F0.wireOp",EDGE,"E1")}),-1.0]])]});
            extrude(context, id + "F1", {"entities" : qUnion([Q0]), "depth" : 1 * mm, "offsetDistance" : 25 * mm});
        }
    });
